# Revit family: 9218445e-7d8a-4c24-a478-a28abc50ba1e
name_source: partatom
category: Plumbing Fixtures
revit_build: Autodesk Revit 2016 (Build: 20161004_0715(x64)
units: mm (PartAtom-declared; Revit-internal decimal feet)

## family parameters
Cut with Voids When Loaded = No
Host = Face
OmniClass Number = 23.45.05.14.14
OmniClass Title = Sinks/Lavatories
Part Type = Normal
Room Calculation Point = No
Round Connector Dimension = Use Diameter
Shared = No

## types (1)
- Not a Type - See Type Catalog
    1L_SS1L = No
    1NL_SS1NL = No
    1NR_SS1NR = No
    1N_SS1N = No
    1R_SS1R = No
    1_SS1 = No
    4N_SS4N = No
    4_SS4 = No
    8N_SS8N = No
    8_SS8 = No
    ADA Compliant = Yes
    Assembly Code = D2010400
    CW Connection = No
    Cold Water Inlet = Cold Water Inlet
    Date Modified = 08/20/2018
    Default Elevation = 34"
    Drain Included = No
    Finish = Default
    HW Connection = No
    Height = 6 9/16"
    Hot Water Inlet = Hot Water Inlet
    Length = 21 15/16"
    Manufacturer = KOHLER Co.
    MasterFormat 1995 = 15410
    MasterFormat 2004 = 22.41.16
    Material = Vitreous china
    Product Documentation Link = http://www.us.kohler.com
    Product Name = Brenham
    Product Page URL = http://www.us.kohler.com
    Type = 0
    URL = https://www.us.kohler.com
    Vent Connection = No
    Waste Connection = Yes
    Waste Water Outlet = Waste Water Outlet
    Width = 19 3/4"

## geometry (parser evidence)
native form markers: Sweep x4
no freeform markers — native parametric forms only
